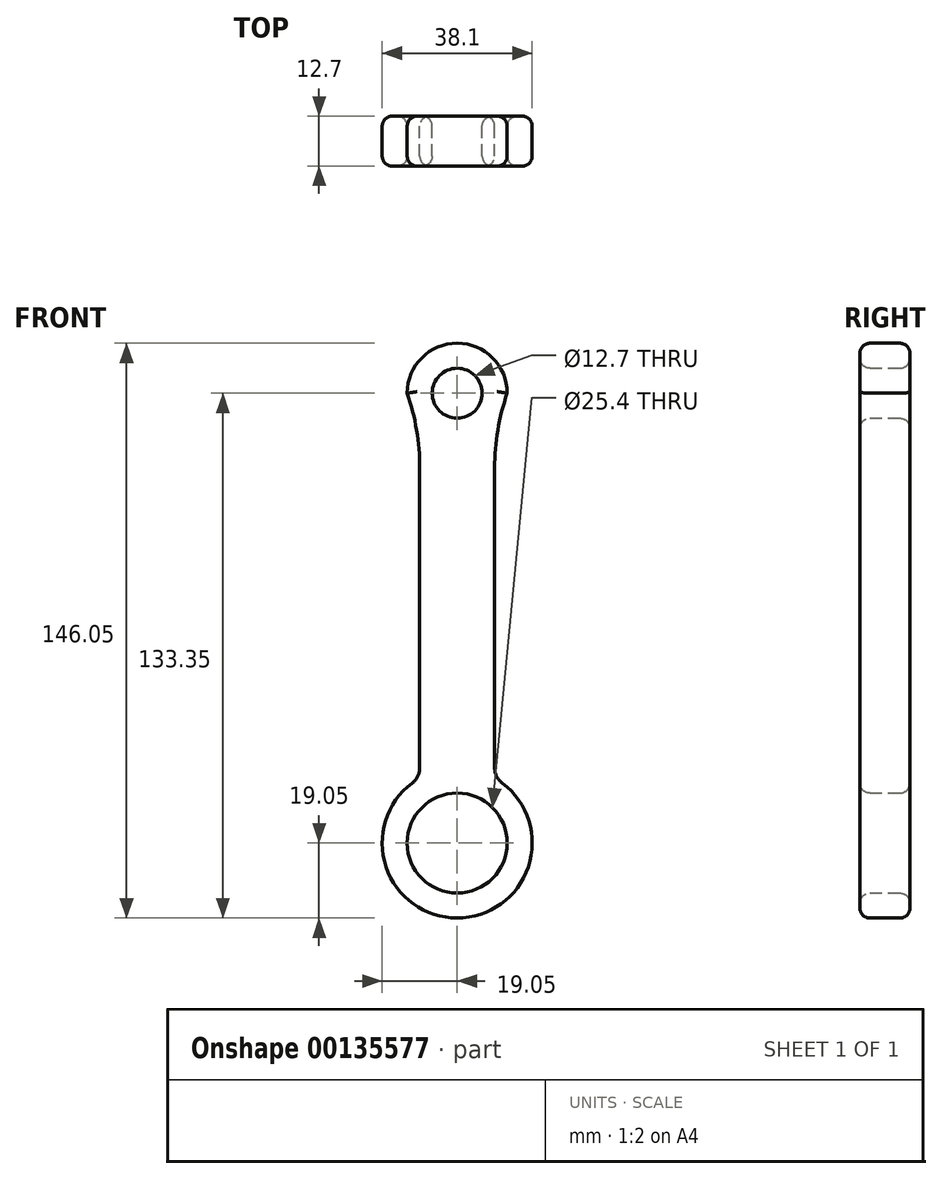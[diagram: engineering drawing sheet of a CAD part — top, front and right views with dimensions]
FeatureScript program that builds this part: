
annotation { "Feature Type Name" : "Feature", "Feature Type Description" : "" }
export const myFeature = defineFeature(function(context is Context, id is Id, definition is map)
    precondition{}
    {
        {
            var Q0;
            Q0=qCreatedBy(makeId("Front.planeOp"),FACE);
            var sketch = newSketch(context, id + "F0", { "sketchPlane" : qUnion([Q0])});
            skCircle(sketch, "E0", {"center": v(0, 0) * mm, "radius": 6.35 * mm});
            skArc(sketch, "E1", {"start": v(12.7, 0) * mm, "mid": v(0, 12.7) * mm, "end": v(-12.7, 0) * mm});
            skCircle(sketch, "E2", {"center": v(0, -114.3) * mm, "radius": 12.7 * mm});
            skArc(sketch, "E3", {"start": v(-11.46, -99.09) * mm, "mid": v(0, -133.35) * mm, "end": v(11.46, -99.09) * mm});
            skLineSegment(sketch, "E4.left", {"start": v(-9.53, -19) * mm, "end": v(-9.52, -95.2) * mm});
            skLineSegment(sketch, "E4.right", {"start": v(9.53, -19) * mm, "end": v(9.53, -95.2) * mm});
            skArc(sketch, "E5", {"start": v(-9.52, -19) * mm, "mid": v(-10.32, -9.37) * mm, "end": v(-12.7, 0) * mm});
            skArc(sketch, "E6", {"start": v(12.7, 0) * mm, "mid": v(10.32, -9.37) * mm, "end": v(9.53, -19) * mm});
            skArc(sketch, "E7", {"start": v(-11.46, -99.09) * mm, "mid": v(-10.04, -97.37) * mm, "end": v(-9.52, -95.2) * mm});
            skArc(sketch, "E8", {"start": v(9.53, -95.2) * mm, "mid": v(10.04, -97.37) * mm, "end": v(11.46, -99.09) * mm});
            skSolve(sketch);
        }
        {
            var Q0;
            Q0 = qSketchRegion(id + "F0", true);
            extrude(context, id + "F1", {"entities" : qUnion([Q0]), "depth" : 12.7 * mm});
        }
        {
            var Q0;
            Q0=makeQuery(id+"F1.opExtrude","CAP_FACE",FACE,{"disambiguationData":[OSD([sQuery(id+"F0.wireOp",EDGE,"E0"),sQuery(id+"F0.wireOp",EDGE,"E1"),sQuery(id+"F0.wireOp",EDGE,"E2"),sQuery(id+"F0.wireOp",EDGE,"E3"),sQuery(id+"F0.wireOp",EDGE,"E4.left"),sQuery(id+"F0.wireOp",EDGE,"E4.right"),sQuery(id+"F0.wireOp",EDGE,"E5"),sQuery(id+"F0.wireOp",EDGE,"E6"),sQuery(id+"F0.wireOp",EDGE,"E7"),sQuery(id+"F0.wireOp",EDGE,"E8")])],"isStart":false});
            var Q1;
            Q1=makeQuery(id+"F1.opExtrude","CAP_FACE",FACE,{"disambiguationData":[OSD([sQuery(id+"F0.wireOp",EDGE,"E0"),sQuery(id+"F0.wireOp",EDGE,"E1"),sQuery(id+"F0.wireOp",EDGE,"E2"),sQuery(id+"F0.wireOp",EDGE,"E3"),sQuery(id+"F0.wireOp",EDGE,"E4.left"),sQuery(id+"F0.wireOp",EDGE,"E4.right"),sQuery(id+"F0.wireOp",EDGE,"E5"),sQuery(id+"F0.wireOp",EDGE,"E6"),sQuery(id+"F0.wireOp",EDGE,"E7"),sQuery(id+"F0.wireOp",EDGE,"E8")])],"isStart":true});
            fillet(context, id + "F2", {"entities" : qUnion([Q0, Q1]), "radius" : 2.54 * mm, "tangentPropagation" : true, "allowEdgeOverflow" : false});
        }
    });
